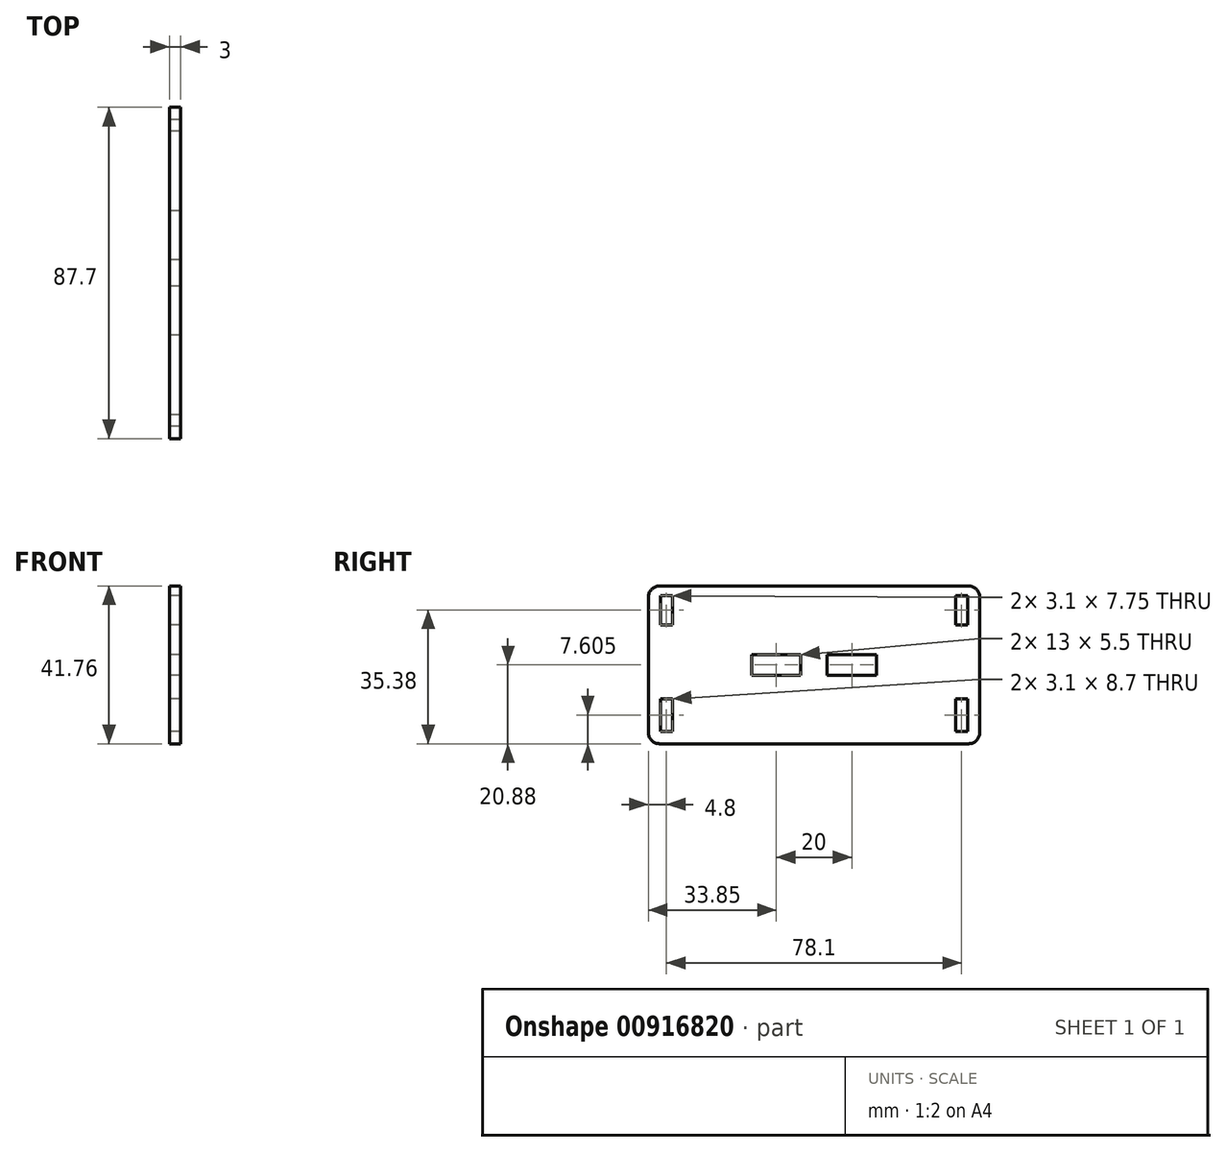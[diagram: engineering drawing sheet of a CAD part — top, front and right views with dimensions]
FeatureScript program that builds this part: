
annotation { "Feature Type Name" : "Feature", "Feature Type Description" : "" }
export const myFeature = defineFeature(function(context is Context, id is Id, definition is map)
    precondition{}
    {
        {
            var Q0;
            Q0=qCreatedBy(makeId("Right.planeOp"),FACE);
            var sketch = newSketch(context, id + "F0", { "sketchPlane" : qUnion([Q0])});
            skLineSegment(sketch, "E0.bottom", {"start": v(-43.85, 20.88) * mm, "end": v(43.85, 20.88) * mm});
            skLineSegment(sketch, "E0.top", {"start": v(-43.85, -20.88) * mm, "end": v(43.85, -20.88) * mm});
            skLineSegment(sketch, "E0.left", {"start": v(-43.85, 20.87) * mm, "end": v(-43.85, -20.87) * mm});
            skLineSegment(sketch, "E0.right", {"start": v(43.85, 20.88) * mm, "end": v(43.85, -20.88) * mm});
            skLineSegment(sketch, "E1", {"start": v(0, 20.88) * mm, "end": v(0, -20.88) * mm, "construction": true});
            skLineSegment(sketch, "E2", {"start": v(-43.85, 0) * mm, "end": v(43.85, 0) * mm, "construction": true});
            skLineSegment(sketch, "E3.bottom", {"start": v(-40.6, 18.38) * mm, "end": v(-37.5, 18.38) * mm});
            skLineSegment(sketch, "E3.top", {"start": v(-40.6, 10.63) * mm, "end": v(-37.5, 10.63) * mm});
            skLineSegment(sketch, "E3.left", {"start": v(-40.6, 18.38) * mm, "end": v(-40.6, 10.63) * mm});
            skLineSegment(sketch, "E3.right", {"start": v(-37.5, 18.38) * mm, "end": v(-37.5, 10.63) * mm});
            skLineSegment(sketch, "E4.MirrorCS", {"start": v(40.6, 18.38) * mm, "end": v(40.6, 10.63) * mm});
            skLineSegment(sketch, "E5.MirrorCS", {"start": v(40.6, 18.38) * mm, "end": v(37.5, 18.38) * mm});
            skLineSegment(sketch, "E6.MirrorCS", {"start": v(40.6, 10.63) * mm, "end": v(37.5, 10.63) * mm});
            skLineSegment(sketch, "E7.MirrorCS", {"start": v(37.5, 18.38) * mm, "end": v(37.5, 10.63) * mm});
            skLineSegment(sketch, "E8.bottom", {"start": v(-40.6, -8.93) * mm, "end": v(-37.5, -8.93) * mm});
            skLineSegment(sketch, "E8.top", {"start": v(-40.6, -17.62) * mm, "end": v(-37.5, -17.62) * mm});
            skLineSegment(sketch, "E8.left", {"start": v(-40.6, -8.93) * mm, "end": v(-40.6, -17.63) * mm});
            skLineSegment(sketch, "E8.right", {"start": v(-37.5, -8.93) * mm, "end": v(-37.5, -17.63) * mm});
            skLineSegment(sketch, "E9.MirrorCS", {"start": v(40.6, -8.92) * mm, "end": v(37.5, -8.92) * mm});
            skLineSegment(sketch, "E10.MirrorCS", {"start": v(40.6, -8.92) * mm, "end": v(40.6, -17.63) * mm});
            skLineSegment(sketch, "E11.MirrorCS", {"start": v(40.6, -17.62) * mm, "end": v(37.5, -17.62) * mm});
            skLineSegment(sketch, "E12.MirrorCS", {"start": v(37.5, -8.93) * mm, "end": v(37.5, -17.62) * mm});
            skLineSegment(sketch, "E13.bottom", {"start": v(-16.5, 2.75) * mm, "end": v(-3.5, 2.75) * mm});
            skLineSegment(sketch, "E13.top", {"start": v(-16.5, -2.75) * mm, "end": v(-3.5, -2.75) * mm});
            skLineSegment(sketch, "E13.left", {"start": v(-16.5, 2.75) * mm, "end": v(-16.5, -2.75) * mm});
            skLineSegment(sketch, "E13.right", {"start": v(-3.5, 2.75) * mm, "end": v(-3.5, -2.75) * mm});
            skLineSegment(sketch, "E14.MirrorCS", {"start": v(3.5, 2.75) * mm, "end": v(3.5, -2.75) * mm});
            skLineSegment(sketch, "E15.MirrorCS", {"start": v(16.5, 2.75) * mm, "end": v(16.5, -2.75) * mm});
            skLineSegment(sketch, "E16.MirrorCS", {"start": v(16.5, -2.75) * mm, "end": v(3.5, -2.75) * mm});
            skLineSegment(sketch, "E17.MirrorCS", {"start": v(16.5, 2.75) * mm, "end": v(3.5, 2.75) * mm});
            skSolve(sketch);
        }
        {
            var Q0;
            Q0 = qSketchRegion(id + "F0", true);
            extrude(context, id + "F1", {"entities" : qUnion([Q0]), "depth" : 3 * mm, "offsetDistance" : 25 * mm});
        }
        {
            var Q0;
            Q0=makeQuery(id+"F1.opExtrude","SWEPT_EDGE",EDGE,{"disambiguationData":[OSD([sQuery(id+"F0.wireOp",EDGE,"E0.bottom"),sQuery(id+"F0.wireOp",EDGE,"E0.left")])]});
            var Q1;
            Q1=makeQuery(id+"F1.opExtrude","SWEPT_EDGE",EDGE,{"disambiguationData":[OSD([sQuery(id+"F0.wireOp",EDGE,"E0.top"),sQuery(id+"F0.wireOp",EDGE,"E0.left")])]});
            var Q2;
            Q2=makeQuery(id+"F1.opExtrude","SWEPT_EDGE",EDGE,{"disambiguationData":[OSD([sQuery(id+"F0.wireOp",EDGE,"E0.bottom"),sQuery(id+"F0.wireOp",EDGE,"E0.right")])]});
            var Q3;
            Q3=makeQuery(id+"F1.opExtrude","SWEPT_EDGE",EDGE,{"disambiguationData":[OSD([sQuery(id+"F0.wireOp",EDGE,"E0.top"),sQuery(id+"F0.wireOp",EDGE,"E0.right")])]});
            fillet(context, id + "F2", {"entities" : qUnion([Q0, Q1, Q2, Q3]), "radius" : 3 * mm, "tangentPropagation" : true, "allowEdgeOverflow" : false});
        }
    });
